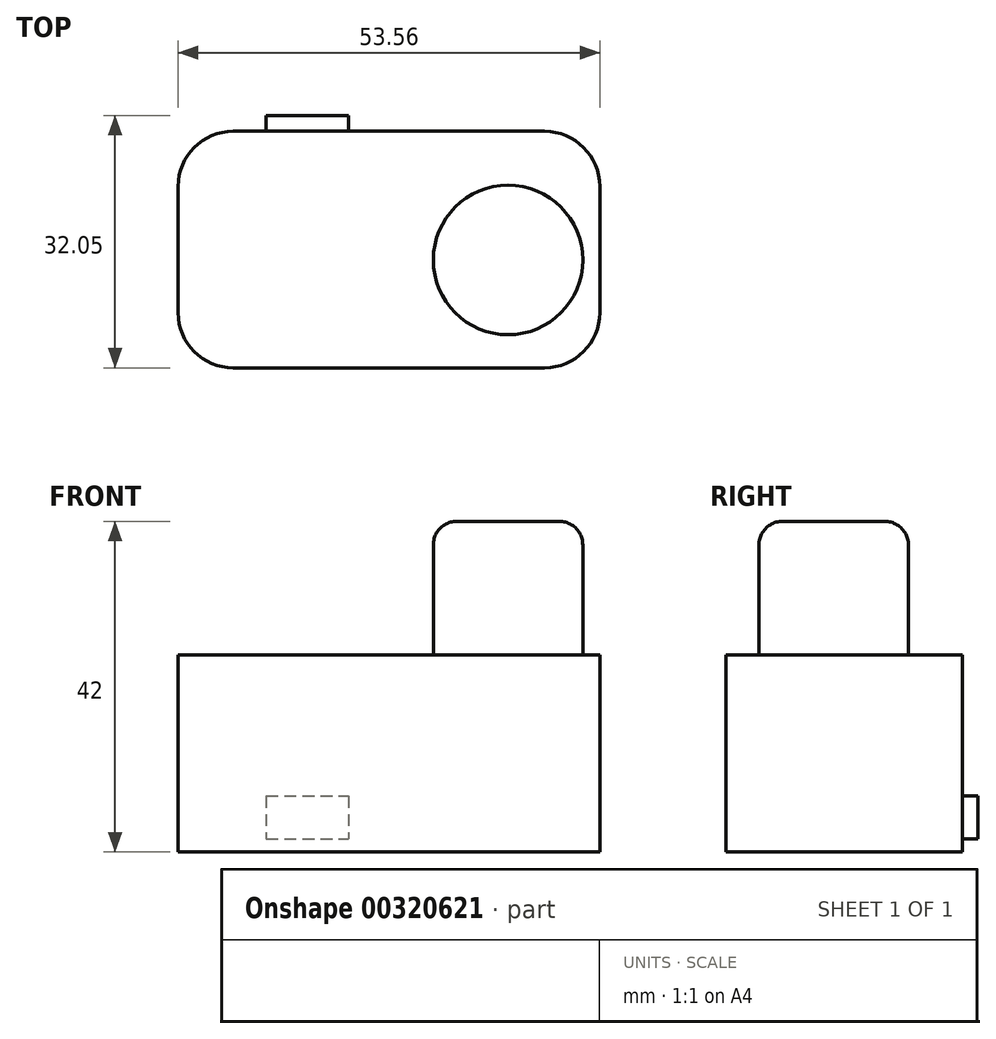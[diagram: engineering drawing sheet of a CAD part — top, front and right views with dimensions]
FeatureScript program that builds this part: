
annotation { "Feature Type Name" : "Feature", "Feature Type Description" : "" }
export const myFeature = defineFeature(function(context is Context, id is Id, definition is map)
    precondition{}
    {
        {
            var Q0;
            Q0=qCreatedBy(makeId("Top.planeOp"),FACE);
            var sketch = newSketch(context, id + "F0", { "sketchPlane" : qUnion([Q0])});
            skLineSegment(sketch, "E0.bottom", {"start": v(-59.9, 36.58) * mm, "end": v(-6.34, 36.58) * mm});
            skLineSegment(sketch, "E0.top", {"start": v(-59.9, 6.53) * mm, "end": v(-6.34, 6.53) * mm});
            skLineSegment(sketch, "E0.left", {"start": v(-59.9, 36.58) * mm, "end": v(-59.9, 6.53) * mm});
            skLineSegment(sketch, "E0.right", {"start": v(-6.34, 36.58) * mm, "end": v(-6.34, 6.53) * mm});
            skSolve(sketch);
        }
        {
            var Q0;
            Q0=makeQuery(id+"F0.imprint","IMPRINT",FACE,{"disambiguationData":[TD([[makeQuery(id+"F0.imprint","IMPRINT",EDGE,{"derivedFrom":sQuery(id+"F0.wireOp",EDGE,"E0.bottom")}),-1.0]])]});
            extrude(context, id + "F1", {"entities" : qUnion([Q0]), "depth" : 25 * mm});
        }
        {
            var Q0;
            Q0=makeQuery(id+"F1.opExtrude","CAP_FACE",FACE,{"disambiguationData":[OSD([sQuery(id+"F0.wireOp",EDGE,"E0.bottom"),sQuery(id+"F0.wireOp",EDGE,"E0.top"),sQuery(id+"F0.wireOp",EDGE,"E0.left"),sQuery(id+"F0.wireOp",EDGE,"E0.right")])],"isStart":false});
            var sketch = newSketch(context, id + "F2", { "sketchPlane" : qUnion([Q0])});
            skCircle(sketch, "E1", {"center": v(-18, 20.24) * mm, "radius": 9.5 * mm});
            skSolve(sketch);
        }
        {
            var Q0;
            Q0=makeQuery(id+"F2.imprint","IMPRINT",FACE,{"disambiguationData":[TD([[makeQuery(id+"F2.imprint","IMPRINT",EDGE,{"derivedFrom":sQuery(id+"F2.wireOp",EDGE,"E1")}),1.0]])]});
            extrude(context, id + "F3", {"entities" : qUnion([Q0]), "operationType" : NewBodyOperationType.ADD, "depth" : 17 * mm});
        }
        {
            var Q0;
            Q0=makeQuery(id+"F3.opExtrude","CAP_EDGE",EDGE,{"disambiguationData":[OSD([sQuery(id+"F2.wireOp",EDGE,"E1")])],"isStart":false});
            fillet(context, id + "F4", {"entities" : qUnion([Q0]), "radius" : 3 * mm, "tangentPropagation" : true, "allowEdgeOverflow" : false});
        }
        {
            var Q0;
            Q0=makeQuery(id+"F1.opExtrude","SWEPT_EDGE",EDGE,{"disambiguationData":[OSD([sQuery(id+"F0.wireOp",EDGE,"E0.bottom"),sQuery(id+"F0.wireOp",EDGE,"E0.right")])]});
            fillet(context, id + "F5", {"entities" : qUnion([Q0]), "radius" : 7 * mm, "tangentPropagation" : true, "allowEdgeOverflow" : false});
        }
        {
            var Q0;
            Q0=makeQuery(id+"F1.opExtrude","SWEPT_EDGE",EDGE,{"disambiguationData":[OSD([sQuery(id+"F0.wireOp",EDGE,"E0.bottom"),sQuery(id+"F0.wireOp",EDGE,"E0.left")])]});
            fillet(context, id + "F6", {"entities" : qUnion([Q0]), "radius" : 7 * mm, "tangentPropagation" : true, "allowEdgeOverflow" : false});
        }
        {
            var Q0;
            Q0=makeQuery(id+"F1.opExtrude","SWEPT_EDGE",EDGE,{"disambiguationData":[OSD([sQuery(id+"F0.wireOp",EDGE,"E0.top"),sQuery(id+"F0.wireOp",EDGE,"E0.left")])]});
            fillet(context, id + "F7", {"entities" : qUnion([Q0]), "radius" : 7 * mm, "tangentPropagation" : true, "allowEdgeOverflow" : false});
        }
        {
            var Q0;
            Q0=makeQuery(id+"F1.opExtrude","SWEPT_EDGE",EDGE,{"disambiguationData":[OSD([sQuery(id+"F0.wireOp",EDGE,"E0.top"),sQuery(id+"F0.wireOp",EDGE,"E0.right")])]});
            fillet(context, id + "F8", {"entities" : qUnion([Q0]), "radius" : 7 * mm, "tangentPropagation" : true, "allowEdgeOverflow" : false});
        }
        {
            var Q0;
            Q0=makeQuery(id+"F3.opExtrude","CAP_FACE",FACE,{"disambiguationData":[OSD([sQuery(id+"F2.wireOp",EDGE,"E1")])],"isStart":false});
            var sketch = newSketch(context, id + "F9", { "sketchPlane" : qUnion([Q0])});
            skCircle(sketch, "E2", {"center": v(-18, 20.24) * mm, "radius": 5.37 * mm});
            skSolve(sketch);
        }
        {
            var Q0;
            Q0=sQuery(id+"F9.wireOp",EDGE,"E2");
            extrude(context, id + "F10", {"bodyType" : ToolBodyType.SURFACE, "surfaceEntities" : qUnion([Q0]), "depth" : 7 * mm});
        }
        {
            var Q0;
            Q0=makeQuery(id+"F1.opExtrude","SWEPT_FACE",FACE,{"disambiguationData":[OSD([sQuery(id+"F0.wireOp",EDGE,"E0.bottom")])]});
            var sketch = newSketch(context, id + "F11", { "sketchPlane" : qUnion([Q0])});
            skLineSegment(sketch, "E3.bottom", {"start": v(48.7, 7.1) * mm, "end": v(38.26, 7.1) * mm});
            skLineSegment(sketch, "E3.top", {"start": v(48.7, 1.68) * mm, "end": v(38.26, 1.68) * mm});
            skLineSegment(sketch, "E3.left", {"start": v(48.7, 7.1) * mm, "end": v(48.7, 1.68) * mm});
            skLineSegment(sketch, "E3.right", {"start": v(38.26, 7.1) * mm, "end": v(38.26, 1.68) * mm});
            skSolve(sketch);
        }
        {
            var Q0;
            Q0=makeQuery(id+"F11.imprint","IMPRINT",FACE,{"disambiguationData":[TD([[makeQuery(id+"F11.imprint","IMPRINT",EDGE,{"derivedFrom":sQuery(id+"F11.wireOp",EDGE,"E3.bottom")}),1.0]])]});
            extrude(context, id + "F12", {"entities" : qUnion([Q0]), "operationType" : NewBodyOperationType.ADD, "depth" : 2 * mm});
        }
    });
